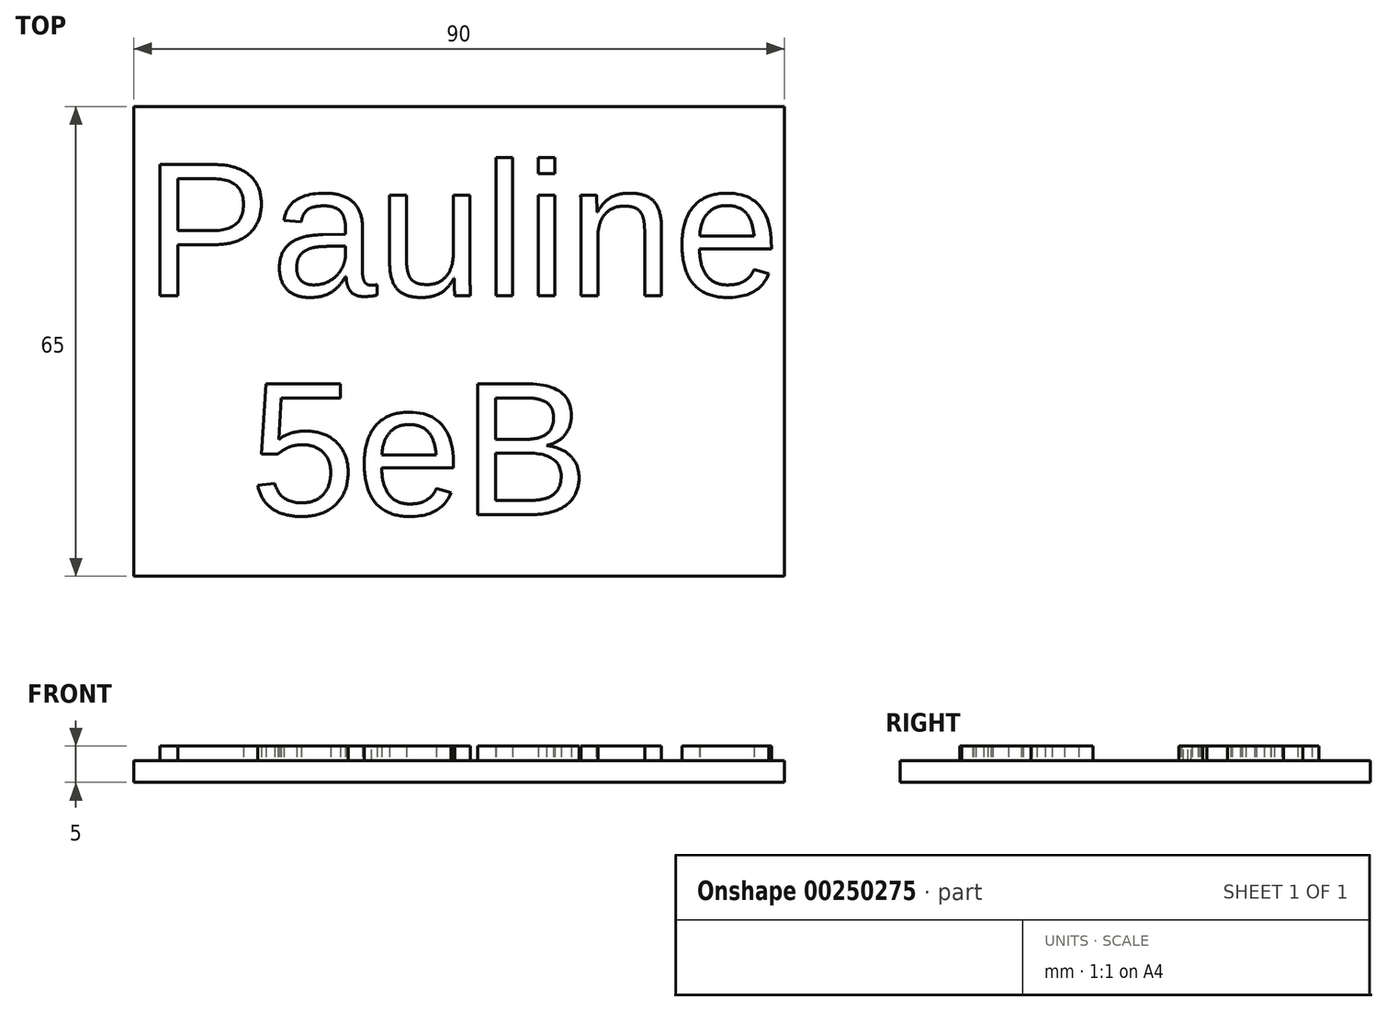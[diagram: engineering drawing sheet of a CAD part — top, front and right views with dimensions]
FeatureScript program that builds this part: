
annotation { "Feature Type Name" : "Feature", "Feature Type Description" : "" }
export const myFeature = defineFeature(function(context is Context, id is Id, definition is map)
    precondition{}
    {
        {
            var Q0;
            Q0=qCreatedBy(makeId("Top.planeOp"),FACE);
            var sketch = newSketch(context, id + "F0", { "sketchPlane" : qUnion([Q0])});
            skLineSegment(sketch, "E0.bottom", {"start": v(0, 0) * mm, "end": v(90, 0) * mm});
            skLineSegment(sketch, "E0.top", {"start": v(0, -65) * mm, "end": v(90, -65) * mm});
            skLineSegment(sketch, "E0.left", {"start": v(0, 0) * mm, "end": v(0, -65) * mm});
            skLineSegment(sketch, "E0.right", {"start": v(90, 0) * mm, "end": v(90, -65) * mm});
            skSolve(sketch);
        }
        {
            var Q0;
            Q0=makeQuery(id+"F0.imprint","IMPRINT",FACE,{"disambiguationData":[TD([[makeQuery(id+"F0.imprint","IMPRINT",EDGE,{"derivedFrom":sQuery(id+"F0.wireOp",EDGE,"E0.bottom")}),-1.0]])]});
            extrude(context, id + "F1", {"entities" : qUnion([Q0]), "depth" : 3 * mm});
        }
        {
            var Q0;
            Q0=makeQuery(id+"F1.opExtrude","CAP_FACE",FACE,{"disambiguationData":[OSD([sQuery(id+"F0.wireOp",EDGE,"E0.bottom"),sQuery(id+"F0.wireOp",EDGE,"E0.top"),sQuery(id+"F0.wireOp",EDGE,"E0.left"),sQuery(id+"F0.wireOp",EDGE,"E0.right")])],"isStart":false});
            var sketch = newSketch(context, id + "F2", { "sketchPlane" : qUnion([Q0])});
            skText(sketch, "E1", { "text": "Pauline\n  5eB", "fontName": "Arimo-Regular.ttf"});
            const initialGuessF2  = {"E1": [0.00147, -0.02617, 1, 0, 0.01897]};
            skSetInitialGuess(sketch, initialGuessF2);
            skSolve(sketch);
        }
        {
            var Q0;
            Q0 = qSketchRegion(id + "F2", true);
            extrude(context, id + "F3", {"entities" : qUnion([Q0]), "operationType" : NewBodyOperationType.ADD, "depth" : 2 * mm});
        }
    });
